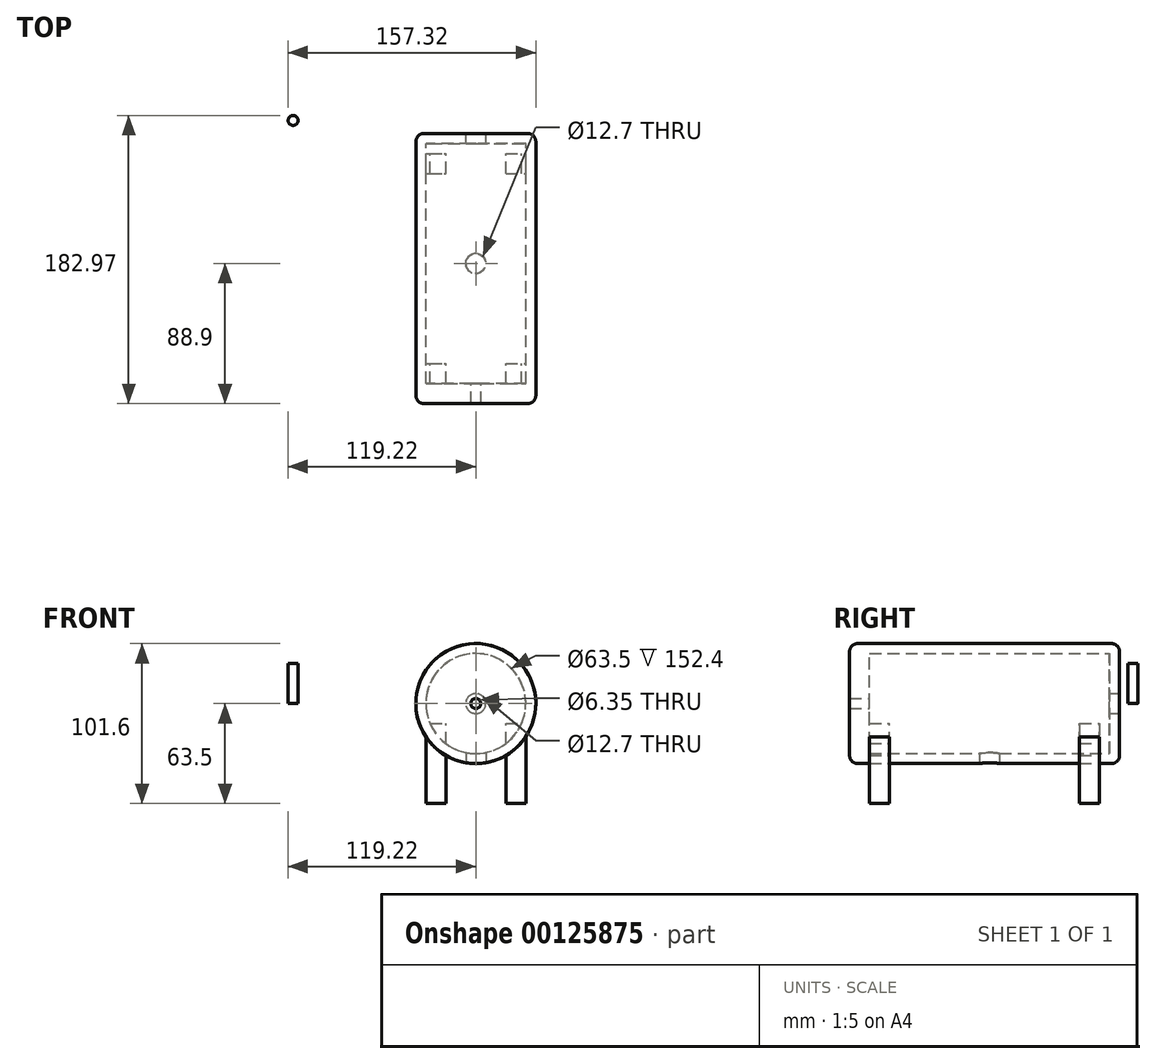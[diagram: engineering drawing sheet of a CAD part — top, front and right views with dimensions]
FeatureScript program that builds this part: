
annotation { "Feature Type Name" : "Feature", "Feature Type Description" : "" }
export const myFeature = defineFeature(function(context is Context, id is Id, definition is map)
    precondition{}
    {
        {
            var Q0;
            Q0=qCreatedBy(makeId("Front.planeOp"),FACE);
            var sketch = newSketch(context, id + "F0", { "sketchPlane" : qUnion([Q0])});
            skCircle(sketch, "E0", {"center": v(0, 0) * mm, "radius": 38.1 * mm});
            skSolve(sketch);
        }
        {
            var Q0;
            Q0 = qSketchRegion(id + "F0", true);
            extrude(context, id + "F1", {"entities" : qUnion([Q0]), "depth" : 6.35 * mm});
        }
        {
            var Q0;
            Q0=makeQuery(id+"F1.opExtrude","CAP_FACE",FACE,{"disambiguationData":[OSD([sQuery(id+"F0.wireOp",EDGE,"E0")])],"isStart":false});
            var sketch = newSketch(context, id + "F2", { "sketchPlane" : qUnion([Q0])});
            skCircle(sketch, "E1", {"center": v(0, 0) * mm, "radius": 38.1 * mm});
            skCircle(sketch, "E2", {"center": v(0, 0) * mm, "radius": 31.75 * mm});
            skSolve(sketch);
        }
        {
            var Q0;
            Q0=makeQuery(id+"F2.imprint","IMPRINT",FACE,{"disambiguationData":[TD([[makeQuery(id+"F2.imprint","IMPRINT",EDGE,{"derivedFrom":sQuery(id+"F2.wireOp",EDGE,"E1")}),1.0]])]});
            extrude(context, id + "F3", {"entities" : qUnion([Q0]), "operationType" : NewBodyOperationType.ADD, "depth" : 152.4 * mm});
        }
        {
            var Q0;
            Q0=makeQuery(id+"F3.opExtrude","CAP_FACE",FACE,{"disambiguationData":[OSD([sQuery(id+"F2.wireOp",EDGE,"E1"),sQuery(id+"F2.wireOp",EDGE,"E2")])],"isStart":false});
            var sketch = newSketch(context, id + "F4", { "sketchPlane" : qUnion([Q0])});
            skCircle(sketch, "E3", {"center": v(0, 0) * mm, "radius": 38.1 * mm});
            skCircle(sketch, "E4", {"center": v(0, 0) * mm, "radius": 3.18 * mm});
            skSolve(sketch);
        }
        {
            var Q0;
            Q0 = qSketchRegion(id + "F4", true);
            extrude(context, id + "F5", {"entities" : qUnion([Q0]), "operationType" : NewBodyOperationType.ADD, "depth" : 12.7 * mm});
        }
        {
            var Q0;
            Q0=makeQuery(id+"F1.opExtrude","CAP_FACE",FACE,{"disambiguationData":[OSD([sQuery(id+"F0.wireOp",EDGE,"E0")])],"isStart":true});
            var sketch = newSketch(context, id + "F6", { "sketchPlane" : qUnion([Q0])});
            skCircle(sketch, "E5", {"center": v(0, 0) * mm, "radius": 6.35 * mm});
            skSolve(sketch);
        }
        {
            var Q0;
            Q0 = qSketchRegion(id + "F6", true);
            extrude(context, id + "F7", {"entities" : qUnion([Q0]), "operationType" : NewBodyOperationType.REMOVE, "oppositeDirection" : true, "depth" : 25.4 * mm});
        }
        {
            var Q0;
            Q0=makeQuery(id+"F1.opExtrude","CAP_EDGE",EDGE,{"disambiguationData":[OSD([sQuery(id+"F0.wireOp",EDGE,"E0")])],"isStart":true});
            var Q1;
            Q1=makeQuery(id+"F5.opExtrude","CAP_EDGE",EDGE,{"disambiguationData":[OSD([sQuery(id+"F4.wireOp",EDGE,"E3")])],"isStart":false});
            fillet(context, id + "F8", {"entities" : qUnion([Q0, Q1]), "radius" : 5.08 * mm, "tangentPropagation" : true, "allowEdgeOverflow" : false});
        }
        {
            var Q0;
            Q0=qCreatedBy(makeId("Top.planeOp"),FACE);
            cPlane(context, id + "F9", {"entities" : qUnion([Q0]), "cplaneType" : CPlaneType.OFFSET, "offset" : 12.7 * mm, "oppositeDirection" : true, "width" : 152.4 * mm, "height" : 152.4 * mm});
        }
        {
            var Q0;
            Q0=qCreatedBy(id+"F9.planeOp",FACE);
            var sketch = newSketch(context, id + "F10", { "sketchPlane" : qUnion([Q0])});
            skLineSegment(sketch, "E6.bottom", {"start": v(-31.75, -158.75) * mm, "end": v(-19.05, -158.75) * mm});
            skLineSegment(sketch, "E6.top", {"start": v(-31.75, -146.05) * mm, "end": v(-19.05, -146.05) * mm});
            skLineSegment(sketch, "E6.left", {"start": v(-31.75, -158.75) * mm, "end": v(-31.75, -146.05) * mm});
            skLineSegment(sketch, "E6.right", {"start": v(-19.05, -158.75) * mm, "end": v(-19.05, -146.05) * mm});
            skLineSegment(sketch, "E7.bottom", {"start": v(19.05, -158.75) * mm, "end": v(31.75, -158.75) * mm});
            skLineSegment(sketch, "E7.top", {"start": v(19.05, -146.05) * mm, "end": v(31.75, -146.05) * mm});
            skLineSegment(sketch, "E7.left", {"start": v(19.05, -158.75) * mm, "end": v(19.05, -146.05) * mm});
            skLineSegment(sketch, "E7.right", {"start": v(31.75, -158.75) * mm, "end": v(31.75, -146.05) * mm});
            skLineSegment(sketch, "E8.bottom", {"start": v(-31.75, -25.4) * mm, "end": v(-19.05, -25.4) * mm});
            skLineSegment(sketch, "E8.top", {"start": v(-31.75, -12.7) * mm, "end": v(-19.05, -12.7) * mm});
            skLineSegment(sketch, "E8.left", {"start": v(-31.75, -25.4) * mm, "end": v(-31.75, -12.7) * mm});
            skLineSegment(sketch, "E8.right", {"start": v(-19.05, -25.4) * mm, "end": v(-19.05, -12.7) * mm});
            skLineSegment(sketch, "E9.bottom", {"start": v(19.05, -25.4) * mm, "end": v(31.75, -25.4) * mm});
            skLineSegment(sketch, "E9.top", {"start": v(19.05, -12.7) * mm, "end": v(31.75, -12.7) * mm});
            skLineSegment(sketch, "E9.left", {"start": v(19.05, -25.4) * mm, "end": v(19.05, -12.7) * mm});
            skLineSegment(sketch, "E9.right", {"start": v(31.75, -25.4) * mm, "end": v(31.75, -12.7) * mm});
            skCircle(sketch, "E10", {"center": v(0, -82.55) * mm, "radius": 6.35 * mm});
            skLineSegment(sketch, "E11", {"start": v(-38.1, -166.37) * mm, "end": v(-38.1, -5.08) * mm});
            skLineSegment(sketch, "E12", {"start": v(38.1, -5.08) * mm, "end": v(38.1, -166.37) * mm});
            skSolve(sketch);
        }
        {
            var Q0;
            Q0 = qSketchRegion(id + "F10", true);
            extrude(context, id + "F11", {"entities" : qUnion([Q0]), "operationType" : NewBodyOperationType.ADD, "oppositeDirection" : true, "depth" : 25.4 * mm});
        }
        {
            var Q0;
            Q0=makeQuery(id+"F11.opExtrude","CAP_FACE",FACE,{"disambiguationData":[OSD([sQuery(id+"F10.wireOp",EDGE,"E6.bottom"),sQuery(id+"F10.wireOp",EDGE,"E6.top"),sQuery(id+"F10.wireOp",EDGE,"E6.left"),sQuery(id+"F10.wireOp",EDGE,"E6.right")])],"isStart":false});
            var Q1;
            Q1=makeQuery(id+"F11.opExtrude","CAP_FACE",FACE,{"disambiguationData":[OSD([sQuery(id+"F10.wireOp",EDGE,"E8.bottom"),sQuery(id+"F10.wireOp",EDGE,"E8.top"),sQuery(id+"F10.wireOp",EDGE,"E8.left"),sQuery(id+"F10.wireOp",EDGE,"E8.right")])],"isStart":false});
            var Q2;
            Q2=makeQuery(id+"F11.opExtrude","CAP_FACE",FACE,{"disambiguationData":[OSD([sQuery(id+"F10.wireOp",EDGE,"E9.bottom"),sQuery(id+"F10.wireOp",EDGE,"E9.top"),sQuery(id+"F10.wireOp",EDGE,"E9.left"),sQuery(id+"F10.wireOp",EDGE,"E9.right")])],"isStart":false});
            var Q3;
            Q3=makeQuery(id+"F11.opExtrude","CAP_FACE",FACE,{"disambiguationData":[OSD([sQuery(id+"F10.wireOp",EDGE,"E7.bottom"),sQuery(id+"F10.wireOp",EDGE,"E7.top"),sQuery(id+"F10.wireOp",EDGE,"E7.left"),sQuery(id+"F10.wireOp",EDGE,"E7.right")])],"isStart":false});
            extrude(context, id + "F12", {"entities" : qUnion([Q0, Q1, Q2, Q3]), "operationType" : NewBodyOperationType.ADD, "depth" : 25.4 * mm});
        }
        {
            var Q0;
            Q0=makeQuery(id+"F11.opExtrude","CAP_FACE",FACE,{"disambiguationData":[OSD([sQuery(id+"F10.wireOp",EDGE,"E10")])],"isStart":false});
            extrude(context, id + "F13", {"entities" : qUnion([Q0]), "operationType" : NewBodyOperationType.ADD, "oppositeDirection" : true, "depth" : 25.4 * mm});
        }
        {
            var Q0;
            Q0=makeQuery(id+"F11.opExtrude","CAP_FACE",FACE,{"disambiguationData":[OSD([sQuery(id+"F10.wireOp",EDGE,"E10")])],"isStart":false});
            var sketch = newSketch(context, id + "F14", { "sketchPlane" : qUnion([Q0])});
            skSolve(sketch);
        }
        {
            var Q0;
            Q0 = qSketchRegion(id + "F14", true);
            var Q1;
            {var subQ0=makeQuery(id+"F11.opExtrude","CAP_EDGE",EDGE,{"disambiguationData":[OSD([sQuery(id+"F10.wireOp",EDGE,"E10")])],"isStart":false});Q1=makeQuery(id+"F14.imprint","IMPRINT",FACE,{"disambiguationData":[TD([[makeQuery(id+"F14.imprint","IMPRINT",EDGE,{"derivedFrom":makeQuery(id+"F11.boolean.opBoolean","SPLIT",EDGE,{"disambiguationData":[OD(0.0)],"derivedFrom":subQ0})}),-1.0]])]});}
            extrude(context, id + "F15", {"entities" : qUnion([Q0, Q1]), "operationType" : NewBodyOperationType.ADD, "oppositeDirection" : true, "depth" : 25.4 * mm});
        }
        {
            var Q0;
            Q0=makeQuery(id+"F11.opExtrude","CAP_FACE",FACE,{"disambiguationData":[OSD([sQuery(id+"F10.wireOp",EDGE,"E10")])],"isStart":false});
            var sketch = newSketch(context, id + "F16", { "sketchPlane" : qUnion([Q0])});
            skCircle(sketch, "E13", {"center": v(0, 82.55) * mm, "radius": 6.35 * mm});
            skSolve(sketch);
        }
        {
            var Q0;
            Q0 = qSketchRegion(id + "F16", true);
            extrude(context, id + "F17", {"entities" : qUnion([Q0]), "operationType" : NewBodyOperationType.REMOVE, "oppositeDirection" : true, "depth" : 25.4 * mm});
        }
        {
            var Q0;
            Q0=qCreatedBy(makeId("Top.planeOp"),FACE);
            var sketch = newSketch(context, id + "F18", { "sketchPlane" : qUnion([Q0])});
            skCircle(sketch, "E14", {"center": v(-116.04, 8.34) * mm, "radius": 3.18 * mm});
            skSolve(sketch);
        }
        {
            var Q0;
            Q0 = qSketchRegion(id + "F18", true);
            extrude(context, id + "F19", {"entities" : qUnion([Q0]), "depth" : 25.4 * mm});
        }
    });
